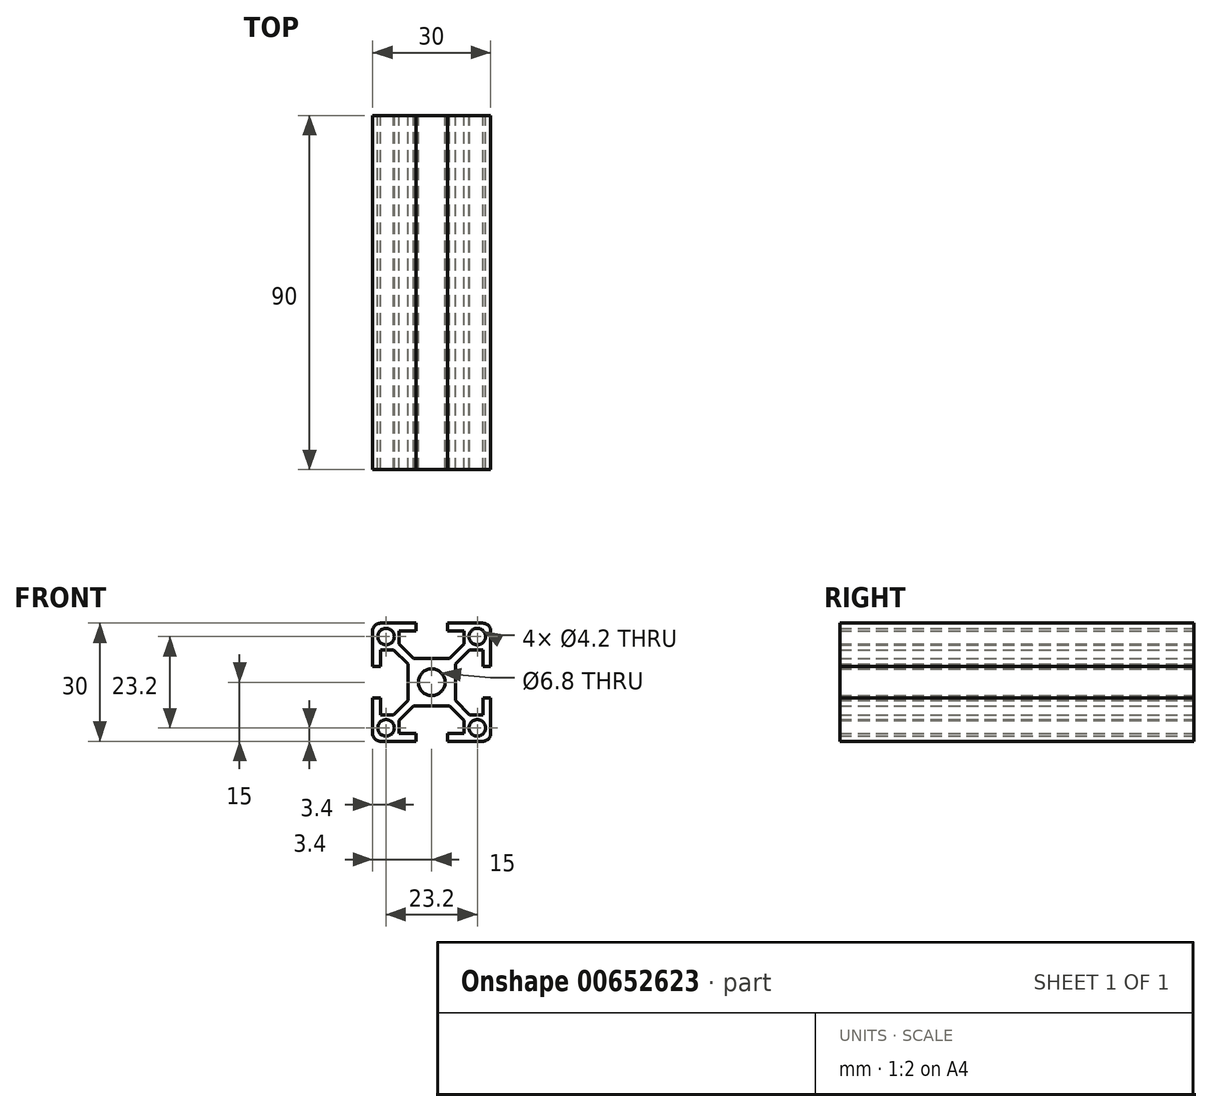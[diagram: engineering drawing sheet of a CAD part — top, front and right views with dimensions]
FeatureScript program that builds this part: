
annotation { "Feature Type Name" : "Feature", "Feature Type Description" : "" }
export const myFeature = defineFeature(function(context is Context, id is Id, definition is map)
    precondition{}
    {
        {
            var Q0;
            Q0=qCreatedBy(makeId("Front.planeOp"),FACE);
            var sketch = newSketch(context, id + "F0", { "sketchPlane" : qUnion([Q0])});
            skLineSegment(sketch, "E0", {"start": v(0, 6) * mm, "end": v(-4.59, 6) * mm});
            skLineSegment(sketch, "E1", {"start": v(-4.59, 6) * mm, "end": v(-8.25, 9.66) * mm});
            skLineSegment(sketch, "E2", {"start": v(-8.25, 9.66) * mm, "end": v(-8.25, 13) * mm});
            skLineSegment(sketch, "E3", {"start": v(-8.25, 13) * mm, "end": v(-4, 13) * mm});
            skLineSegment(sketch, "E4", {"start": v(-4, 13) * mm, "end": v(-4, 15) * mm});
            skLineSegment(sketch, "E5", {"start": v(-4, 15) * mm, "end": v(-13, 15) * mm});
            skLineSegment(sketch, "E6", {"start": v(-15, 13) * mm, "end": v(-15, 4) * mm});
            skLineSegment(sketch, "E7", {"start": v(-15, 4) * mm, "end": v(-13, 4) * mm});
            skLineSegment(sketch, "E8", {"start": v(-13, 4) * mm, "end": v(-13, 8.25) * mm});
            skLineSegment(sketch, "E9", {"start": v(-13, 8.25) * mm, "end": v(-9.66, 8.25) * mm});
            skLineSegment(sketch, "E10", {"start": v(-9.66, 8.25) * mm, "end": v(-6, 4.59) * mm});
            skLineSegment(sketch, "E11", {"start": v(-6, 4.59) * mm, "end": v(-6, 0) * mm});
            skLineSegment(sketch, "E12", {"start": v(-6, 0) * mm, "end": v(0, 0) * mm, "construction": true});
            skLineSegment(sketch, "E13", {"start": v(0, 0) * mm, "end": v(0, 6) * mm, "construction": true});
            skArc(sketch, "E14", {"start": v(0, 3.4) * mm, "mid": v(-2.4, 2.4) * mm, "end": v(-3.4, 0) * mm});
            skCircle(sketch, "E15", {"center": v(-11.6, 11.6) * mm, "radius": 2.1 * mm});
            skLineSegment(sketch, "E16", {"start": v(0, 0) * mm, "end": v(-7.38, 7.38) * mm, "construction": true});
            skLineSegment(sketch, "E17.1.0", {"start": v(-8.25, -13) * mm, "end": v(-8.25, -9.66) * mm});
            skLineSegment(sketch, "E17.1.1", {"start": v(-4, -15) * mm, "end": v(-4, -13) * mm});
            skLineSegment(sketch, "E17.1.2", {"start": v(-4, -13) * mm, "end": v(-8.25, -13) * mm});
            skLineSegment(sketch, "E17.1.3", {"start": v(-15, -4) * mm, "end": v(-15, -13) * mm});
            skLineSegment(sketch, "E17.1.4", {"start": v(-8.25, -9.66) * mm, "end": v(-4.59, -6) * mm});
            skLineSegment(sketch, "E17.1.5", {"start": v(-13, -15) * mm, "end": v(-4, -15) * mm});
            skLineSegment(sketch, "E17.1.6", {"start": v(-4.59, -6) * mm, "end": v(0, -6) * mm});
            skLineSegment(sketch, "E17.1.7", {"start": v(0, -6) * mm, "end": v(0, 0) * mm, "construction": true});
            skLineSegment(sketch, "E17.1.8", {"start": v(0, 0) * mm, "end": v(-6, 0) * mm, "construction": true});
            skLineSegment(sketch, "E17.1.9", {"start": v(-13, -4) * mm, "end": v(-15, -4) * mm});
            skLineSegment(sketch, "E17.1.10", {"start": v(-13, -8.25) * mm, "end": v(-13, -4) * mm});
            skArc(sketch, "E17.1.11", {"start": v(-3.4, 0) * mm, "mid": v(-2.4, -2.4) * mm, "end": v(0, -3.4) * mm});
            skLineSegment(sketch, "E17.1.12", {"start": v(-9.66, -8.25) * mm, "end": v(-13, -8.25) * mm});
            skLineSegment(sketch, "E17.1.13", {"start": v(0, 0) * mm, "end": v(-7.38, -7.38) * mm, "construction": true});
            skLineSegment(sketch, "E17.1.14", {"start": v(-6, -4.59) * mm, "end": v(-9.66, -8.25) * mm});
            skCircle(sketch, "E17.1.15", {"center": v(-11.6, -11.6) * mm, "radius": 2.1 * mm});
            skLineSegment(sketch, "E17.1.16", {"start": v(-6, 0) * mm, "end": v(-6, -4.59) * mm});
            skLineSegment(sketch, "E17.2.0", {"start": v(13, -8.25) * mm, "end": v(9.66, -8.25) * mm});
            skLineSegment(sketch, "E17.2.1", {"start": v(15, -4) * mm, "end": v(13, -4) * mm});
            skLineSegment(sketch, "E17.2.2", {"start": v(13, -4) * mm, "end": v(13, -8.25) * mm});
            skLineSegment(sketch, "E17.2.3", {"start": v(4, -15) * mm, "end": v(13, -15) * mm});
            skLineSegment(sketch, "E17.2.4", {"start": v(9.66, -8.25) * mm, "end": v(6, -4.59) * mm});
            skLineSegment(sketch, "E17.2.5", {"start": v(15, -13) * mm, "end": v(15, -4) * mm});
            skLineSegment(sketch, "E17.2.6", {"start": v(6, -4.59) * mm, "end": v(6, 0) * mm});
            skLineSegment(sketch, "E17.2.7", {"start": v(6, 0) * mm, "end": v(0, 0) * mm, "construction": true});
            skLineSegment(sketch, "E17.2.8", {"start": v(0, 0) * mm, "end": v(0, -6) * mm, "construction": true});
            skLineSegment(sketch, "E17.2.9", {"start": v(4, -13) * mm, "end": v(4, -15) * mm});
            skLineSegment(sketch, "E17.2.10", {"start": v(8.25, -13) * mm, "end": v(4, -13) * mm});
            skArc(sketch, "E17.2.11", {"start": v(0, -3.4) * mm, "mid": v(2.4, -2.4) * mm, "end": v(3.4, 0) * mm});
            skLineSegment(sketch, "E17.2.12", {"start": v(8.25, -9.66) * mm, "end": v(8.25, -13) * mm});
            skLineSegment(sketch, "E17.2.13", {"start": v(0, 0) * mm, "end": v(7.38, -7.38) * mm, "construction": true});
            skLineSegment(sketch, "E17.2.14", {"start": v(4.59, -6) * mm, "end": v(8.25, -9.66) * mm});
            skCircle(sketch, "E17.2.15", {"center": v(11.6, -11.6) * mm, "radius": 2.1 * mm});
            skLineSegment(sketch, "E17.2.16", {"start": v(0, -6) * mm, "end": v(4.59, -6) * mm});
            skLineSegment(sketch, "E17.3.0", {"start": v(8.25, 13) * mm, "end": v(8.25, 9.66) * mm});
            skLineSegment(sketch, "E17.3.1", {"start": v(4, 15) * mm, "end": v(4, 13) * mm});
            skLineSegment(sketch, "E17.3.2", {"start": v(4, 13) * mm, "end": v(8.25, 13) * mm});
            skLineSegment(sketch, "E17.3.3", {"start": v(15, 4) * mm, "end": v(15, 13) * mm});
            skLineSegment(sketch, "E17.3.4", {"start": v(8.25, 9.66) * mm, "end": v(4.59, 6) * mm});
            skLineSegment(sketch, "E17.3.5", {"start": v(13, 15) * mm, "end": v(4, 15) * mm});
            skLineSegment(sketch, "E17.3.6", {"start": v(4.59, 6) * mm, "end": v(0, 6) * mm});
            skLineSegment(sketch, "E17.3.7", {"start": v(0, 6) * mm, "end": v(0, 0) * mm, "construction": true});
            skLineSegment(sketch, "E17.3.8", {"start": v(0, 0) * mm, "end": v(6, 0) * mm, "construction": true});
            skLineSegment(sketch, "E17.3.9", {"start": v(13, 4) * mm, "end": v(15, 4) * mm});
            skLineSegment(sketch, "E17.3.10", {"start": v(13, 8.25) * mm, "end": v(13, 4) * mm});
            skArc(sketch, "E17.3.11", {"start": v(3.4, 0) * mm, "mid": v(2.4, 2.4) * mm, "end": v(0, 3.4) * mm});
            skLineSegment(sketch, "E17.3.12", {"start": v(9.66, 8.25) * mm, "end": v(13, 8.25) * mm});
            skLineSegment(sketch, "E17.3.13", {"start": v(0, 0) * mm, "end": v(7.38, 7.38) * mm, "construction": true});
            skLineSegment(sketch, "E17.3.14", {"start": v(6, 4.59) * mm, "end": v(9.66, 8.25) * mm});
            skCircle(sketch, "E17.3.15", {"center": v(11.6, 11.6) * mm, "radius": 2.1 * mm});
            skLineSegment(sketch, "E17.3.16", {"start": v(6, 0) * mm, "end": v(6, 4.59) * mm});
            skPoint(sketch, "E18.visualSharp", {"position": v(-15, 15) * mm});
            skArc(sketch, "E18.filletArc", {"start": v(-13, 15) * mm, "mid": v(-14.41, 14.41) * mm, "end": v(-15, 13) * mm});
            skPoint(sketch, "E19.visualSharp", {"position": v(15, 15) * mm});
            skArc(sketch, "E19.filletArc", {"start": v(15, 13) * mm, "mid": v(14.41, 14.41) * mm, "end": v(13, 15) * mm});
            skPoint(sketch, "E20.visualSharp", {"position": v(15, -15) * mm});
            skArc(sketch, "E20.filletArc", {"start": v(13, -15) * mm, "mid": v(14.41, -14.41) * mm, "end": v(15, -13) * mm});
            skPoint(sketch, "E21.visualSharp", {"position": v(-15, -15) * mm});
            skArc(sketch, "E21.filletArc", {"start": v(-15, -13) * mm, "mid": v(-14.41, -14.41) * mm, "end": v(-13, -15) * mm});
            skSolve(sketch);
        }
        {
            var Q0;
            Q0 = qSketchRegion(id + "F0", true);
            extrude(context, id + "F1", {"entities" : qUnion([Q0]), "depth" : 90 * mm, "offsetDistance" : 25 * mm});
        }
    });
